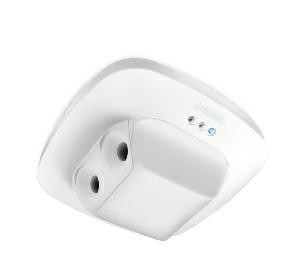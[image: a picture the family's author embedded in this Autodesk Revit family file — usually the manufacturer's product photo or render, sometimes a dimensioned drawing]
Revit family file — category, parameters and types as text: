
# Revit family: single_us_059507
name_source: partatom
category: Elektroinstallationen
revit_build: Autodesk Revit 2016 (Build: 20190508_0715(x64)
units: mm (PartAtom-declared; Revit-internal decimal feet)

## family parameters
Basisbauteil = Fläche
Beim Laden mit Abzugskörper schneiden = Nein
Bemaßung runder Anschluss = Durchmesser verwenden
Beschriftungsausrichtung beibehalten = Nein
Gemeinsam genutzt = Nein
Raumberechnungspunkt = Nein
Teiletyp = Normal

## types (1)
- Single US
    Apparent Load = 0 VA
    Beschreibung = Type: Presence detector; Dimensions (L x W x H): 73 x 120 x 120 mm; Mains power supply: 24 – 29 V; Sensor Technology: Ultrasonic; Application, place: Indoors; Application, room: corridor / aisle, stairwell, Indoors; Installation site: ceiling; Installation: Concealed wiring; Electronic scalability: Yes; Mechanical scalability: No; Mounting height: 2,50 – 3,50 m; Optimum mounting height: 2,8 m; Detection angle: 180 °; Angle of aperture: 180 °; Sneak-by guard: Yes; Reach, radial: 10 x 3 m (30 m²); Reach, tangential: 10 x 3 m (30 m²); Twilight setting TEACH: Yes; Twilight setting: 10 – 1000 lx; Time setting: 0 sec – 1092 min; Basic light level function: Yes; Basic light level function time: 1-30 min, all day; KNX functions: Photo-cell controller, Basic light level function, Light level, HVAC output, Constant-lighting control, Light output 4x, Presence output, Day / night function; With bus coupling: Yes; Settings via: ETS software, Remote control, Bus, Smart Remote; Interconnection: Yes; IP-rating: IP20; Material: Plastic; Ambient temperature: -25 – 55 °C; Colour: white; Colour, RAL: 9010; Manufacturer's Warranty: 5 years; Version: KNX; PU1, EAN: 4007841059507
    Height = 0 mm  [stored 0 ft]
    Hersteller = Steinel
    Length = 73 mm
    Maximum range = 10.662 m
    ModVariant = Nein
    Modell = 059507
    Mounting Place = Ceiling
    Mounting Type = Recessed
    Number of Poles = 1
    OnlyDefault = Ja
    Power Factor = 1
    Product Name = Single US
    Product group = Presence detector
    ProductGroupID = 4
    Protection Class = Protection class
    Protection Degree = IP 20
    RlxData = <blob elided: 121313 chars, md5=392db66a>
    Sensor characteristics = Stretched
    Sensor type = Passive (infrared)
    SensorDataFile = <blob elided: 159730 chars, md5=e60cc4e0>
    Type of entry = Motion
    Typenbild = produkt1_059507.jpg
    Typenkommentare = Product without accessories
    URL = http://relux.com
    VarID = ---
    Voltage = 0 V
    Vorgabe-Ansicht = 1800 mm
    Weight = 0.00 kg
    Width = 120 mm  [stored 0.393701 ft]

note: [stored X ft] marks values corroborated as IEEE doubles in the binary element streams (Revit-internal decimal feet)

## geometry (parser evidence)
native form markers: Blend x4, Sweep x17
no freeform markers — native parametric forms only
